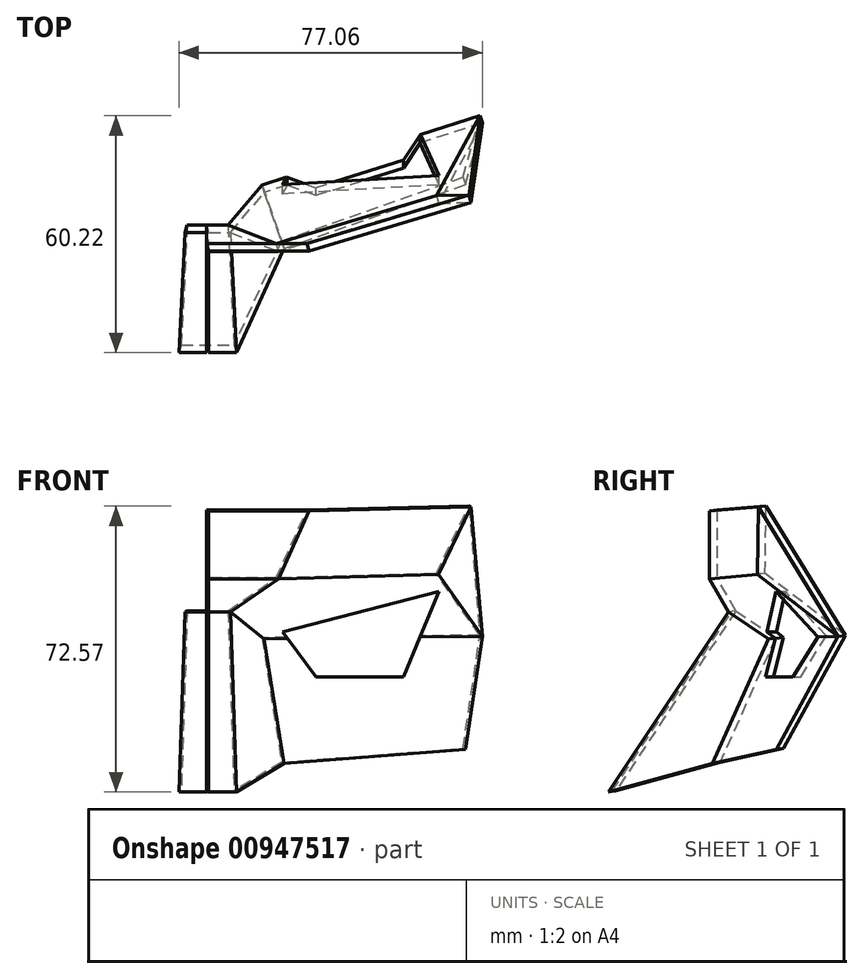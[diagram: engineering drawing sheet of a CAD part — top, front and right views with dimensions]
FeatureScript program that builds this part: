
annotation { "Feature Type Name" : "Feature", "Feature Type Description" : "" }
export const myFeature = defineFeature(function(context is Context, id is Id, definition is map)
    precondition{}
    {
        {
            assignVariable(context, id + "F0", {"variableType" : VariableType.LENGTH, "name" : "t", "lengthValue" : 2 * mm});
        }
        {
            var Q0;
            Q0=qCreatedBy(makeId("Top.planeOp"),FACE);
            var sketch = newSketch(context, id + "F1", { "sketchPlane" : qUnion([Q0])});
            skLineSegment(sketch, "E0", {"start": v(0, -40) * mm, "end": v(7.5, -40) * mm});
            skLineSegment(sketch, "E1", {"start": v(7.5, -40) * mm, "end": v(22.5, 0) * mm});
            skSolve(sketch);
        }
        {
            var Q0;
            Q0=qCreatedBy(makeId("Right.planeOp"),FACE);
            var sketch = newSketch(context, id + "F2", { "sketchPlane" : qUnion([Q0])});
            skLineSegment(sketch, "E2", {"start": v(-40, 0) * mm, "end": v(0, 60) * mm});
            skSolve(sketch);
        }
        {
            var Q0;
            Q0=sQuery(id+"F2.wireOp",EDGE,"E2");
            var Q1;
            Q1=sQuery(id+"F1.wireOp",EDGE,"E0");
            cPlane(context, id + "F3", {"entities" : qUnion([Q0, Q1]), "cplaneType" : CPlaneType.LINE_ANGLE, "offset" : 25 * mm, "angle" : 0 * degree, "width" : 150 * mm, "height" : 150 * mm});
        }
        {
            var Q0;
            Q0=qCreatedBy(id+"F3.planeOp",FACE);
            var sketch = newSketch(context, id + "F4", { "sketchPlane" : qUnion([Q0])});
            skLineSegment(sketch, "E3.bottom", {"start": v(0, 49.92) * mm, "end": v(-5.5, 49.92) * mm});
            skLineSegment(sketch, "E3.top", {"start": v(0, -5.08) * mm, "end": v(-7, -5.08) * mm});
            skLineSegment(sketch, "E3.left", {"start": v(0, 49.92) * mm, "end": v(0, -5.08) * mm});
            skLineSegment(sketch, "E3.right", {"start": v(-5.5, 49.92) * mm, "end": v(-7, -5.08) * mm});
            skSolve(sketch);
        }
        {
            var Q0;
            Q0=sQuery(id+"F4.wireOp",EDGE,"E3.right");
            var Q1;
            Q1=qCreatedBy(id+"F3.planeOp",FACE);
            cPlane(context, id + "F5", {"entities" : qUnion([Q0, Q1]), "cplaneType" : CPlaneType.LINE_ANGLE, "offset" : 25 * mm, "angle" : 55 * degree, "oppositeDirection" : true, "width" : 150 * mm, "height" : 150 * mm});
        }
        {
            var Q0;
            Q0=qCreatedBy(id+"F5.planeOp",FACE);
            var sketch = newSketch(context, id + "F6", { "sketchPlane" : qUnion([Q0])});
            skLineSegment(sketch, "E4", {"start": v(-21.49, 10.5) * mm, "end": v(12.97, 53.4) * mm});
            skLineSegment(sketch, "E5", {"start": v(12.97, 53.4) * mm, "end": v(24.46, 43.75) * mm});
            skLineSegment(sketch, "E6", {"start": v(24.46, 43.75) * mm, "end": v(8.44, 12.63) * mm});
            skLineSegment(sketch, "E7", {"start": v(8.44, 12.63) * mm, "end": v(-21.49, 10.5) * mm});
            skSolve(sketch);
        }
        {
            var Q0;
            Q0=sQuery(id+"F6.wireOp",EDGE,"E6");
            var Q1;
            Q1=qCreatedBy(id+"F5.planeOp",FACE);
            cPlane(context, id + "F7", {"entities" : qUnion([Q0, Q1]), "cplaneType" : CPlaneType.LINE_ANGLE, "offset" : 25 * mm, "angle" : 40 * degree, "width" : 150 * mm, "height" : 150 * mm});
        }
        {
            var Q0;
            Q0=qCreatedBy(id+"F7.planeOp",FACE);
            var sketch = newSketch(context, id + "F8", { "sketchPlane" : qUnion([Q0])});
            skLineSegment(sketch, "E8", {"start": v(-9.66, 52.07) * mm, "end": v(-14.8, 17.45) * mm});
            skLineSegment(sketch, "E9", {"start": v(-14.8, 17.45) * mm, "end": v(-62.7, 27.81) * mm});
            skLineSegment(sketch, "E10", {"start": v(-62.7, 27.81) * mm, "end": v(-67.17, 60.5) * mm});
            skLineSegment(sketch, "E11", {"start": v(-67.17, 60.5) * mm, "end": v(-46.89, 57.53) * mm});
            skLineSegment(sketch, "E12", {"start": v(-46.89, 57.53) * mm, "end": v(-42.63, 48.48) * mm});
            skLineSegment(sketch, "E13", {"start": v(-42.63, 48.48) * mm, "end": v(-28.3, 46.35) * mm});
            skLineSegment(sketch, "E14", {"start": v(-28.3, 46.35) * mm, "end": v(-18.56, 53.38) * mm});
            skLineSegment(sketch, "E15", {"start": v(-18.56, 53.38) * mm, "end": v(-9.66, 52.07) * mm});
            skLineSegment(sketch, "E16", {"start": v(-46.89, 57.53) * mm, "end": v(-18.56, 53.38) * mm, "construction": true});
            skSolve(sketch);
        }
        {
            var Q0;
            Q0=sQuery(id+"F6.wireOp",VERTEX,"E5.end");
            var Q1;
            Q1=sQuery(id+"F8.wireOp",VERTEX,"E14.end");
            var Q2;
            Q2=sQuery(id+"F4.wireOp",VERTEX,"E3.bottom.end");
            cPlane(context, id + "F9", {"entities" : qUnion([Q0, Q1, Q2]), "cplaneType" : CPlaneType.THREE_POINT, "offset" : 25 * mm, "width" : 150 * mm, "height" : 150 * mm});
        }
        {
            var Q0;
            Q0=qCreatedBy(id+"F9.planeOp",FACE);
            var sketch = newSketch(context, id + "F10", { "sketchPlane" : qUnion([Q0])});
            skLineSegment(sketch, "E17", {"start": v(23.85, -29.02) * mm, "end": v(32.65, -27.1) * mm});
            skLineSegment(sketch, "E18", {"start": v(32.65, -27.1) * mm, "end": v(43.77, -30) * mm});
            skLineSegment(sketch, "E19", {"start": v(43.77, -30) * mm, "end": v(54.51, -27.6) * mm});
            skLineSegment(sketch, "E20", {"start": v(54.51, -27.6) * mm, "end": v(60.61, -20.99) * mm});
            skLineSegment(sketch, "E21", {"start": v(60.61, -20.99) * mm, "end": v(80.64, -16.62) * mm});
            skLineSegment(sketch, "E22", {"start": v(80.64, -16.62) * mm, "end": v(69.25, -42.2) * mm});
            skLineSegment(sketch, "E23", {"start": v(69.25, -42.2) * mm, "end": v(27.53, -50.3) * mm});
            skLineSegment(sketch, "E24", {"start": v(27.53, -50.3) * mm, "end": v(15.03, -41.14) * mm});
            skLineSegment(sketch, "E25", {"start": v(15.03, -41.14) * mm, "end": v(23.85, -29.02) * mm});
            skSolve(sketch);
        }
        {
            var Q0;
            Q0=sQuery(id+"F2.wireOp",VERTEX,"E2.end");
            var Q1;
            Q1=sQuery(id+"F4.wireOp",VERTEX,"E3.bottom.end");
            var Q2;
            Q2=sQuery(id+"F10.wireOp",VERTEX,"E23.end");
            cPlane(context, id + "F11", {"entities" : qUnion([Q0, Q1, Q2]), "cplaneType" : CPlaneType.THREE_POINT, "offset" : 25 * mm, "width" : 150 * mm, "height" : 150 * mm});
        }
        {
            var Q0;
            Q0=qCreatedBy(id+"F11.planeOp",FACE);
            var sketch = newSketch(context, id + "F12", { "sketchPlane" : qUnion([Q0])});
            skLineSegment(sketch, "E26", {"start": v(0, 52.02) * mm, "end": v(-5.5, 52.02) * mm});
            skLineSegment(sketch, "E27", {"start": v(-5.5, 52.02) * mm, "end": v(-17.7, 61.58) * mm});
            skLineSegment(sketch, "E28", {"start": v(-17.7, 61.58) * mm, "end": v(0, 61.58) * mm});
            skLineSegment(sketch, "E29", {"start": v(0, 61.58) * mm, "end": v(0, 52.02) * mm});
            skSolve(sketch);
        }
        {
            var Q0;
            Q0=qCreatedBy(id+"F11.planeOp",FACE);
            var Q1;
            Q1=sQuery(id+"F12.wireOp",EDGE,"E28");
            cPlane(context, id + "F13", {"entities" : qUnion([Q0, Q1]), "cplaneType" : CPlaneType.LINE_ANGLE, "offset" : 25 * mm, "angle" : 30 * degree, "width" : 150 * mm, "height" : 150 * mm});
        }
        {
            var Q0;
            Q0=qCreatedBy(id+"F13.planeOp",FACE);
            var sketch = newSketch(context, id + "F14", { "sketchPlane" : qUnion([Q0])});
            skLineSegment(sketch, "E30", {"start": v(0, 68.29) * mm, "end": v(17.7, 68.29) * mm});
            skLineSegment(sketch, "E31", {"start": v(17.7, 68.29) * mm, "end": v(25.5, 85.6) * mm});
            skLineSegment(sketch, "E32", {"start": v(25.5, 85.6) * mm, "end": v(0, 85.6) * mm});
            skLineSegment(sketch, "E33", {"start": v(0, 85.6) * mm, "end": v(0, 68.29) * mm});
            skSolve(sketch);
        }
        {
            var Q0;
            Q0=sQuery(id+"F14.wireOp",VERTEX,"E31.end");
            var Q1;
            Q1=sQuery(id+"F10.wireOp",VERTEX,"E23.end");
            var Q2;
            Q2=sQuery(id+"F10.wireOp",VERTEX,"E22.end");
            cPlane(context, id + "F15", {"entities" : qUnion([Q0, Q1, Q2]), "cplaneType" : CPlaneType.THREE_POINT, "offset" : 25 * mm, "width" : 150 * mm, "height" : 150 * mm});
        }
        {
            var Q0;
            Q0=qCreatedBy(id+"F15.planeOp",FACE);
            var sketch = newSketch(context, id + "F16", { "sketchPlane" : qUnion([Q0])});
            skLineSegment(sketch, "E34", {"start": v(-18.22, 68.32) * mm, "end": v(-60.72, 67.82) * mm});
            skLineSegment(sketch, "E35", {"start": v(-60.72, 67.82) * mm, "end": v(-69.37, 84.74) * mm});
            skLineSegment(sketch, "E36", {"start": v(-69.37, 84.74) * mm, "end": v(-26.38, 85.48) * mm});
            skLineSegment(sketch, "E37", {"start": v(-26.38, 85.48) * mm, "end": v(-18.22, 68.32) * mm});
            skSolve(sketch);
        }
        {
            var Q0;
            Q0=sQuery(id+"F10.wireOp",VERTEX,"E22.end");
            var Q1;
            Q1=sQuery(id+"F16.wireOp",VERTEX,"E35.end");
            var Q2;
            Q2=sQuery(id+"F8.wireOp",VERTEX,"E10.end");
            cPlane(context, id + "F17", {"entities" : qUnion([Q0, Q1, Q2]), "cplaneType" : CPlaneType.THREE_POINT, "offset" : 25 * mm, "width" : 150 * mm, "height" : 150 * mm});
        }
        {
            var Q0;
            Q0=qCreatedBy(id+"F17.planeOp",FACE);
            var sketch = newSketch(context, id + "F18", { "sketchPlane" : qUnion([Q0])});
            skLineSegment(sketch, "E38", {"start": v(46.78, 78.3) * mm, "end": v(20.42, 87.75) * mm});
            skLineSegment(sketch, "E39", {"start": v(20.42, 87.75) * mm, "end": v(20.68, 106.75) * mm});
            skLineSegment(sketch, "E40", {"start": v(20.68, 106.75) * mm, "end": v(46.78, 78.3) * mm});
            skSolve(sketch);
        }
        {
            var Q0;
            Q0=makeQuery(id+"F16.imprint","IMPRINT",FACE,{"disambiguationData":[TD([[makeQuery(id+"F16.imprint","IMPRINT",EDGE,{"derivedFrom":sQuery(id+"F16.wireOp",EDGE,"E34")}),-1.0]])]});
            var Q1;
            Q1=makeQuery(id+"F14.imprint","IMPRINT",FACE,{"disambiguationData":[TD([[makeQuery(id+"F14.imprint","IMPRINT",EDGE,{"derivedFrom":sQuery(id+"F14.wireOp",EDGE,"E30")}),1.0]])]});
            var Q2;
            Q2=makeQuery(id+"F12.imprint","IMPRINT",FACE,{"disambiguationData":[TD([[makeQuery(id+"F12.imprint","IMPRINT",EDGE,{"derivedFrom":sQuery(id+"F12.wireOp",EDGE,"E26")}),-1.0]])]});
            var Q3;
            Q3=makeQuery(id+"F10.imprint","IMPRINT",FACE,{"disambiguationData":[TD([[makeQuery(id+"F10.imprint","IMPRINT",EDGE,{"derivedFrom":sQuery(id+"F10.wireOp",EDGE,"E17")}),-1.0]])]});
            var Q4;
            Q4=makeQuery(id+"F4.imprint","IMPRINT",FACE,{"disambiguationData":[TD([[makeQuery(id+"F4.imprint","IMPRINT",EDGE,{"derivedFrom":sQuery(id+"F4.wireOp",EDGE,"E3.bottom")}),1.0]])]});
            var Q5;
            Q5=makeQuery(id+"F6.imprint","IMPRINT",FACE,{"disambiguationData":[TD([[makeQuery(id+"F6.imprint","IMPRINT",EDGE,{"derivedFrom":sQuery(id+"F6.wireOp",EDGE,"E4")}),-1.0]])]});
            var Q6;
            Q6=makeQuery(id+"F8.imprint","IMPRINT",FACE,{"disambiguationData":[TD([[makeQuery(id+"F8.imprint","IMPRINT",EDGE,{"derivedFrom":sQuery(id+"F8.wireOp",EDGE,"E8")}),-1.0]])]});
            var Q7;
            Q7=makeQuery(id+"F18.imprint","IMPRINT",FACE,{"disambiguationData":[TD([[makeQuery(id+"F18.imprint","IMPRINT",EDGE,{"derivedFrom":sQuery(id+"F18.wireOp",EDGE,"E38")}),-1.0]])]});
            extrude(context, id + "F19", {"entities" : qUnion([Q0, Q1, Q2, Q3, Q4, Q5, Q6, Q7]), "depth" : getVariable(context, 't') / 2, "offsetDistance" : 25 * mm, "hasSecondDirection" : true, "secondDirectionOppositeDirection" : true, "secondDirectionDepth" : getVariable(context, 't') / 2});
        }
        {
            var Q0;
            Q0=qCreatedBy(makeId("Front.planeOp"),FACE);
            var sketch = newSketch(context, id + "F20", { "sketchPlane" : qUnion([Q0])});
            skLineSegment(sketch, "E41", {"start": v(19, 54.73) * mm, "end": v(27.5, 43.35) * mm});
            skLineSegment(sketch, "E42", {"start": v(27.5, 43.35) * mm, "end": v(49.82, 43.35) * mm});
            skLineSegment(sketch, "E43", {"start": v(49.82, 43.35) * mm, "end": v(58.75, 64.99) * mm});
            skLineSegment(sketch, "E44", {"start": v(58.75, 64.99) * mm, "end": v(19, 54.73) * mm});
            skSolve(sketch);
        }
        {
            var Q0;
            Q0 = qSketchRegion(id + "F20", true);
            extrude(context, id + "F21", {"entities" : qUnion([Q0]), "operationType" : NewBodyOperationType.REMOVE, "endBound" : BoundingType.THROUGH_ALL, "depth" : 25 * mm, "offsetDistance" : 25 * mm, "hasSecondDirection" : true, "secondDirectionBound" : BoundingType.THROUGH_ALL, "secondDirectionOppositeDirection" : true, "secondDirectionDepth" : 25 * mm});
        }
        {
            var Q0;
            Q0=makeQuery(id+"F19.opExtrude","SWEPT_BODY",BODY,{"disambiguationData":[OSD([sQuery(id+"F4.wireOp",EDGE,"E3.bottom"),sQuery(id+"F4.wireOp",EDGE,"E3.top"),sQuery(id+"F4.wireOp",EDGE,"E3.left"),sQuery(id+"F4.wireOp",EDGE,"E3.right")])]});
            var Q1;
            Q1=qCreatedBy(makeId("Right.planeOp"),FACE);
            mirror(context, id + "F22", {"operationType" : NewBodyOperationType.ADD, "entities" : qUnion([Q0]), "mirrorPlane" : qUnion([Q1])});
        }
    });
